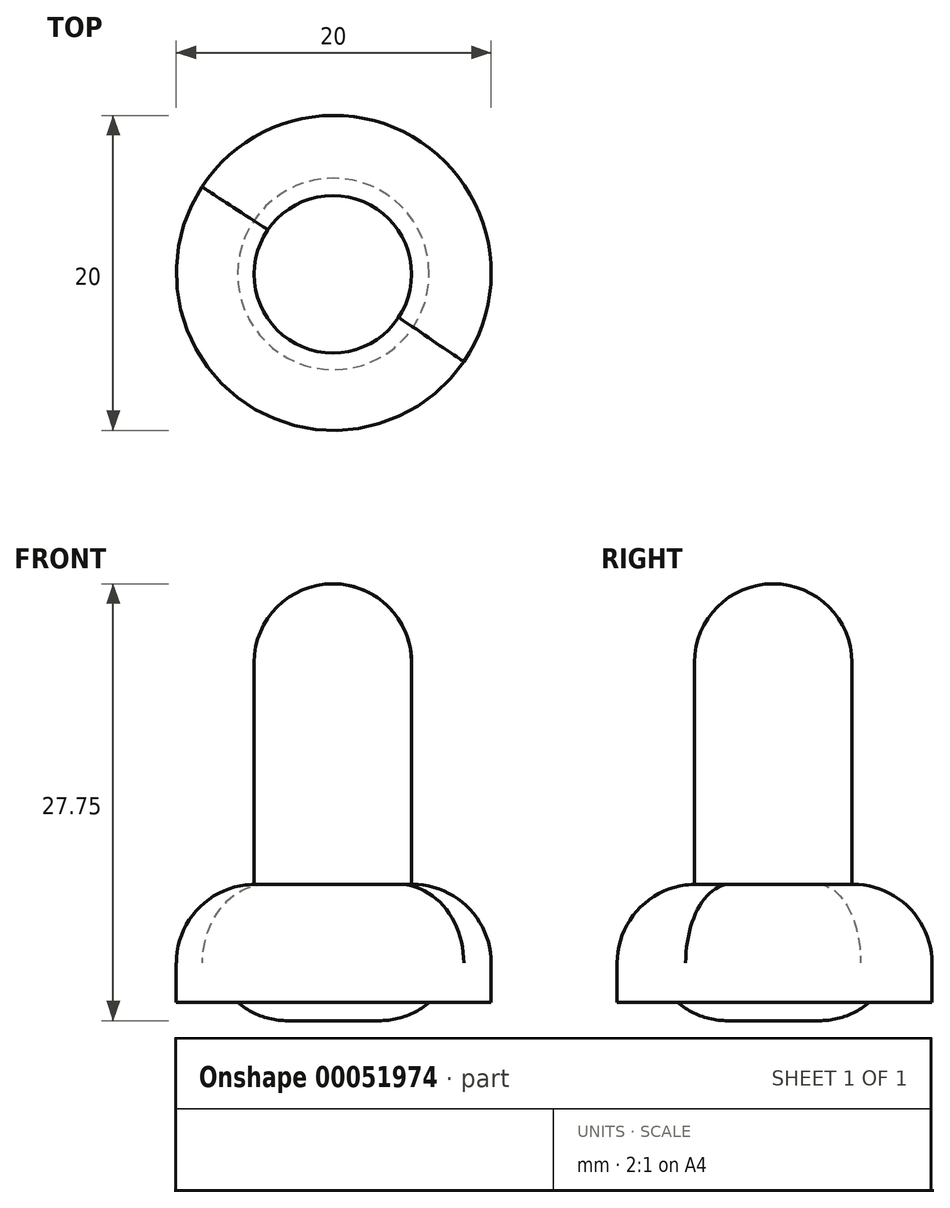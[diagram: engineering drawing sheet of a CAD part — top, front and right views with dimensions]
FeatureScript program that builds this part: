
annotation { "Feature Type Name" : "Feature", "Feature Type Description" : "" }
export const myFeature = defineFeature(function(context is Context, id is Id, definition is map)
    precondition{}
    {
        {
            var Q0;
            Q0=qCreatedBy(makeId("Top.planeOp"),FACE);
            var sketch = newSketch(context, id + "F0", { "sketchPlane" : qUnion([Q0])});
            skCircle(sketch, "E0", {"center": v(-37.38, 38.32) * mm, "radius": 10 * mm});
            skSolve(sketch);
        }
        {
            var Q0;
            Q0 = qSketchRegion(id + "F0", true);
            extrude(context, id + "F1", {"entities" : qUnion([Q0]), "depth" : 7.5 * mm});
        }
        {
            var Q0;
            Q0=qCreatedBy(makeId("Top.planeOp"),FACE);
            var sketch = newSketch(context, id + "F2", { "sketchPlane" : qUnion([Q0])});
            skCircle(sketch, "E1", {"center": v(-37.43, 38.23) * mm, "radius": 5 * mm});
            skSolve(sketch);
        }
        {
            var Q0;
            Q0 = qSketchRegion(id + "F2", true);
            extrude(context, id + "F3", {"entities" : qUnion([Q0]), "operationType" : NewBodyOperationType.ADD, "depth" : 26.6 * mm});
        }
        {
            var Q0;
            Q0=qCreatedBy(makeId("Top.planeOp"),FACE);
            var sketch = newSketch(context, id + "F4", { "sketchPlane" : qUnion([Q0])});
            skCircle(sketch, "E2", {"center": v(-37.4, 38.25) * mm, "radius": 6.08 * mm});
            skSolve(sketch);
        }
        {
            var Q0;
            Q0 = qSketchRegion(id + "F4", true);
            extrude(context, id + "F5", {"entities" : qUnion([Q0]), "operationType" : NewBodyOperationType.ADD, "oppositeDirection" : true, "depth" : 1.15 * mm});
        }
        {
            var Q0;
            Q0=makeQuery(id+"F3.opExtrude","CAP_EDGE",EDGE,{"disambiguationData":[OSD([sQuery(id+"F2.wireOp",EDGE,"E1")])],"isStart":false});
            var Q1;
            Q1=makeQuery(id+"F1.opExtrude","CAP_EDGE",EDGE,{"disambiguationData":[OSD([sQuery(id+"F0.wireOp",EDGE,"E0")])],"isStart":false});
            var Q2;
            Q2=makeQuery(id+"F5.opExtrude","CAP_EDGE",EDGE,{"disambiguationData":[OSD([sQuery(id+"F4.wireOp",EDGE,"E2")])],"isStart":false});
            fillet(context, id + "F6", {"entities" : qUnion([Q0, Q1, Q2]), "radius" : 5 * mm, "tangentPropagation" : true, "allowEdgeOverflow" : false});
        }
    });
